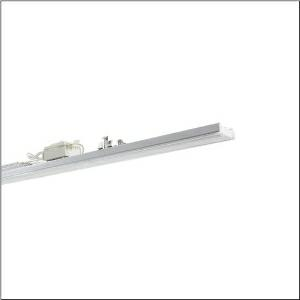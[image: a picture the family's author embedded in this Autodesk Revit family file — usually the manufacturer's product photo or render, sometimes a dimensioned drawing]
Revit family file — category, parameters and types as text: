
# Revit family: licross_11_recessed_ho_51te11dv4m2s
name_source: partatom
category: Lighting Fixtures
units: mm (PartAtom-declared; Revit-internal decimal feet)

## family parameters
Cut with Voids When Loaded = No
Host = Face
Light Source = No
Part Type = Normal
Room Calculation Point = No
Round Connector Dimension = Use Diameter
Shared = No

## types (1)
- --- (1 x LED, 27080 lm, 150.5 W, 4000K)
    Apparent Load = 150 VA
    CIE Flux Codes = 87 95 99 100 100
    Color Rendering = 80
    Color Temperature = 4000K
    Default Elevation = 1800 mm
    Description = Licross 11 Recessed HO, luminaire insert, of sheet steel, galvanised, coil coated, white, length: 2.250mm, width: 66mm, height: 67mm, LED rated luminous flux: 27.080lm, light colour: 840, SDCM (Standard Deviation of Colour Matching)MacAdam ≤ 2 SDCM (initial), control gear: DALI 2, with plug, 5-pole, with phase selection, mains connection: 220..240V, AC, 50/60Hz, rated input power: 151W, internal wiring halogen-free, primary light control with lens, of plastic, primary optical cover: cover, of PMMA, light emission: direct distribution, primary light characteristic: symmetric, protection rating (complete): IP54, insulation class (complete): insulation class I (protective earthing), certification: CE, ENEC, VDE, UKCA, protection symbol: D if used in an environment with non-conductive dust loads with corresponding accessories, impact resistance: IK06, permissible ambient temperature for indoor applications: -40..+35°C, corresponds to IFS (International Featured Standards) requirements for safety and quality in the food industry, reducing of maximum allowable ambient temperature of 5°C with ceiling mounting, LABS conformity tested according to VDMA 24364:2018-05, The light source and the operating device comply with the requirements of the Ecodesign Regulation (EU) 2019/2020 and are replaceable in accordance with this regulation, packaging unit: 1 piece
    Height = 58 mm
    Lamp = 1 x LED
    Lamp Light Flux = 27080 lm
    Lamp Power = 150.5 W
    Lamp count = 1
    Length = 2250 mm
    Luminous efficacy = 180 lm/W
    Manufacturer = Siteco
    ModVariant = No
    Model = 51TE11DV4M2S
    Mounting Place = Ceiling
    Mounting Type = Pendant
    Number of Poles = 1
    OnlyDefault = Yes
    Power Factor = 1
    Product Name = Licross 11 Recessed HO
    Product group = luminaire insert | ceiling pendant
    ProductGroupID = 901
    Protection Class = Protection class I
    Protection Degree = IP 54
    RLX_Detail_Level = 1
    RLX_Emergency_Light_Flux = 0 lm
    RLX_Emergency_Type = 0
    RLX_Emergency_Type_DB = No
    RlxData = <blob elided: 29813 chars, md5=e0ee9500>
    Socket = socket
    Standby Power = 0 W
    System Light Flux = 27079 lm
    System Power = 150 W
    Type Comments = factory setting: luminous flux: 100 % | dim-lin: 254 | 690 mA
    Type Image = l_1296930.jpg
    URL = http://relux.com
    VarID = @adj_100361
    Voltage = 0 V
    Weight = 0.00 kg
    Width = 66 mm

## geometry (parser evidence)
native form markers: Blend x4, Sweep x10
no freeform markers — native parametric forms only
